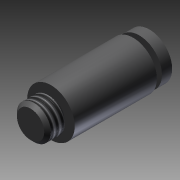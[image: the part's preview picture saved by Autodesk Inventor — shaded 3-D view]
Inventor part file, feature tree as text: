
AUTODESK INVENTOR PART (.ipt)
format: ipt  version: 2016 (Build 200138000, 138)  size: 127,488 bytes
history: native  units: mm
features: sketch x3, revolve x2, thread x1, extrude x1
ambient origin geometry x8: Origin, YZ Plane, XZ Plane, XY Plane, X Axis, Y Axis, Z Axis, Center Point
bodies: Solid1 (feature_tree)
feature tree (7):
  revolve  "Revolution1"  [1 undecoded]
  thread  "Thread1"  [1 undecoded]
  revolve  "Revolution2"  [1 undecoded]
  extrude  "Extrusion1"  [1 undecoded]
  sketch  "Sketch_1"  dims[d0=360.0deg d1=2.019mm d2=0.0mm d3=360.0deg]
  sketch  "Sketch_2"  dims[d4=16.3mm d5=0.0mm]
  sketch  "Sketch_3"
note: 4 required parameter values undecoded (feature->parameter linkage not recoverable at this tier; creation-order binding heuristic only, values carry confidence <= 0.55)